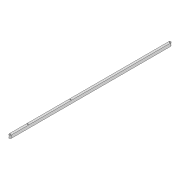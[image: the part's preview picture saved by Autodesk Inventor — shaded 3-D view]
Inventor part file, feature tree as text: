
AUTODESK INVENTOR PART (.ipt)
format: ipt  version: 2022 (Build 260153000, 153)  size: 97,792 bytes
history: native  units: mm
features: extrude x1, sketch x1
ambient origin geometry x8: Origin, YZ Plane, XZ Plane, XY Plane, X Axis, Y Axis, Z Axis, Center Point
bodies: Solid1 (feature_tree)
feature tree (2):
  extrude  "Extrusion1"  Depth=435.595mm
  sketch  "Sketch1"  dims[d0=6.0mm d1=435.595mm d2=3.0mm d3=3.0mm d4=8.0mm d5=0.0mm d20=3.0mm d21=47.52mm d22=3.0mm d23=164.378mm]
